# Revit family: Storage-Mounted-Teknion-BRLL_Full_Solid_Door_Tower_Low_Secondary_Desk-R2018
name_source: partatom
category: Furniture
revit_build: Autodesk Revit 2018 (Build: 20190510_1515(x64)
units: mm (PartAtom-declared; Revit-internal decimal feet)

## family parameters
Always vertical = Yes
Cut with Voids When Loaded = No
OmniClass Number = 23.40.70.14.64.21
OmniClass Title = Systems Furniture
Room Calculation Point = No
Shared = Yes
Work Plane-Based = No

## types (6) — shared parameters
Assembly Code = E2020200
Depth = 17.91 "
Manufacturer = Teknion
Manufacturer Fax = 416.661.4586
Part Number = BRLL
Product Documentation Link = http://www.teknion.com
Product Line = Expansion Casegoods
Product Page URL = http://www.teknion.com
Series = Expansion Casegoods
Sustainability Data = http://www.teknion.com
URL = http://www.teknion.com
Unit Weight URL = http://www.teknion.com
Warranty = http://www.teknion.com
Width = 17.91 "

## per-type parameters (varying)
| type | Description | Has File Drawer and Shelves | Has Shelves | Has Wardrobe | Height | Model |
| File Drawer and Shelves, 18"d x 18"w, 72"h | Tower with Full Solid Door - Low Secondary Desk Mounted, File Drawer and Shelves, 18" Depth, 18" Width, 72" Height | Yes | No | No | 71.582 " | BRLLF181872 |
| File Drawer and Shelves, 18"d x 18"w, 66"h | Tower with Full Solid Door - Low Secondary Desk Mounted, File Drawer and Shelves, 18" Depth, 18" Width, 66" Height | Yes | No | No | 65.34 " | BRLLF181866_ |
| Shelves, 18"d x 18"w, 72"h | Tower with Full Solid Door - Low Secondary Desk Mounted, Shelves, 18" Depth, 18" Width, 72" Height | No | Yes | No | 71.582 " | BRLLS181872 |
| Shelves, 18"d x 18"w, 66"h | Tower with Full Solid Door - Low Secondary Desk Mounted, Shelves, 18" Depth, 18" Width, 66" Height | No | Yes | No | 65.34 " | BRLLS181866_ |
| Wardrobe, 18"d x 18"w, 72"h | Tower with Full Solid Door - Low Secondary Desk Mounted, Wardrobe, 18" Depth, 18" Width, 72" Height | No | No | Yes | 71.582 " | BRLLW181872 |
| Wardrobe, 18"d x 18"w, 66"h | Tower with Full Solid Door - Low Secondary Desk Mounted, Wardrobe, 18" Depth, 18" Width, 66" Height | No | No | Yes | 65.34 " | BRLLW181866_ |

## geometry (parser evidence)
native form markers: Blend x8, Sweep x3
no freeform markers — native parametric forms only
